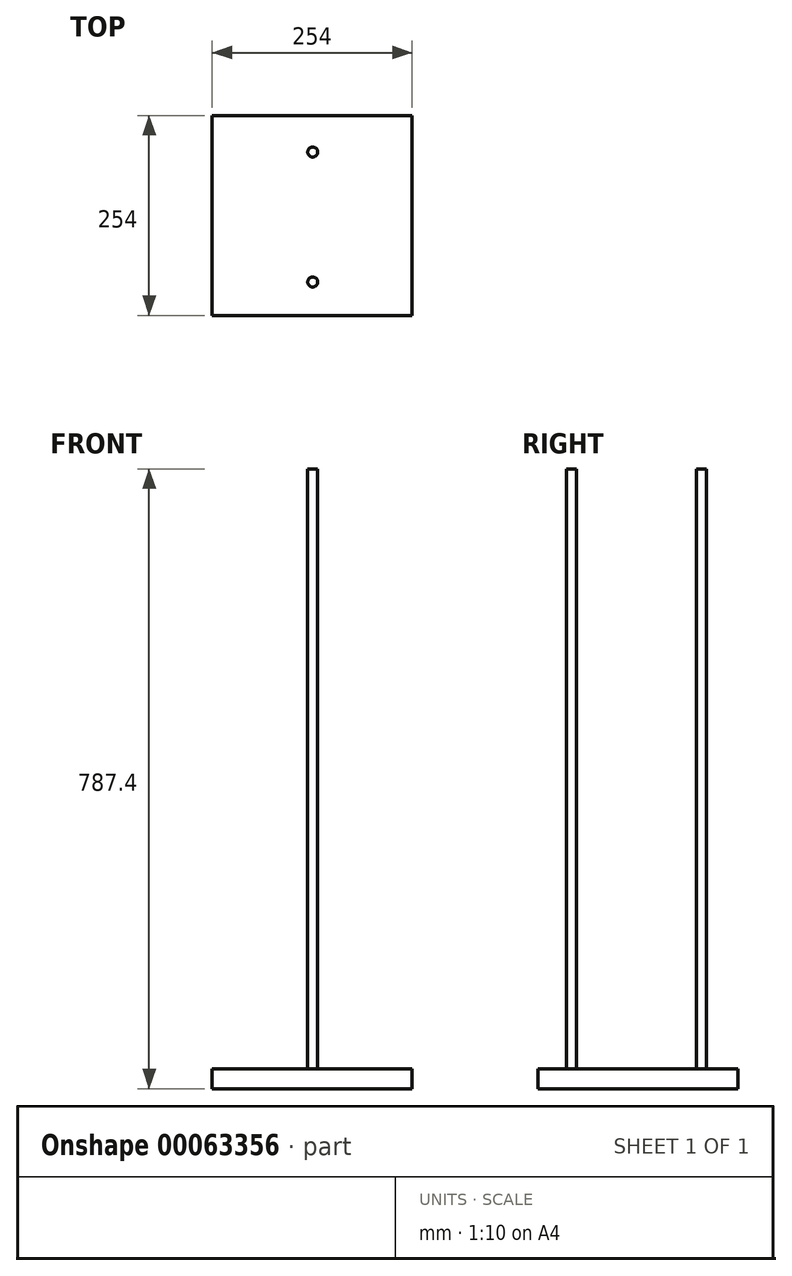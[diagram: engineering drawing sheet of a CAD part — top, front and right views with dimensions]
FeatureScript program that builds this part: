
annotation { "Feature Type Name" : "Feature", "Feature Type Description" : "" }
export const myFeature = defineFeature(function(context is Context, id is Id, definition is map)
    precondition{}
    {
        {
            var Q0;
            Q0=qCreatedBy(makeId("Top.planeOp"),FACE);
            var sketch = newSketch(context, id + "F0", { "sketchPlane" : qUnion([Q0])});
            skLineSegment(sketch, "E0.bottom", {"start": v(-127.78, 129.03) * mm, "end": v(126.22, 129.03) * mm});
            skLineSegment(sketch, "E0.top", {"start": v(-127.78, -124.97) * mm, "end": v(126.22, -124.97) * mm});
            skLineSegment(sketch, "E0.left", {"start": v(-127.78, 129.03) * mm, "end": v(-127.78, -124.97) * mm});
            skLineSegment(sketch, "E0.right", {"start": v(126.22, 129.03) * mm, "end": v(126.22, -124.97) * mm});
            skSolve(sketch);
        }
        {
            var Q0;
            Q0 = qSketchRegion(id + "F0", true);
            extrude(context, id + "F1", {"entities" : qUnion([Q0]), "endBound" : BoundingType.SYMMETRIC, "depth" : 25.4 * mm});
        }
        {
            var Q0;
            Q0=makeQuery(id+"F1.opExtrude","CAP_FACE",FACE,{"disambiguationData":[OSD([sQuery(id+"F0.wireOp",EDGE,"E0.bottom"),sQuery(id+"F0.wireOp",EDGE,"E0.top"),sQuery(id+"F0.wireOp",EDGE,"E0.left"),sQuery(id+"F0.wireOp",EDGE,"E0.right")])],"isStart":false});
            var sketch = newSketch(context, id + "F2", { "sketchPlane" : qUnion([Q0])});
            skCircle(sketch, "E1", {"center": v(0, -82.55) * mm, "radius": 6.35 * mm});
            skCircle(sketch, "E2", {"center": v(0, 82.55) * mm, "radius": 6.35 * mm});
            skSolve(sketch);
        }
        {
            var Q0;
            Q0 = qSketchRegion(id + "F2", true);
            extrude(context, id + "F3", {"entities" : qUnion([Q0]), "operationType" : NewBodyOperationType.ADD, "depth" : 762 * mm});
        }
        {
            var Q0;
            Q0=qCreatedBy(makeId("Right.planeOp"),FACE);
            var sketch = newSketch(context, id + "F4", { "sketchPlane" : qUnion([Q0])});
            skLineSegment(sketch, "E3", {"start": v(-76.2, 787.4) * mm, "end": v(-76.2, 25.4) * mm, "construction": true});
            skLineSegment(sketch, "E4", {"start": v(76.2, 25.4) * mm, "end": v(76.2, 787.4) * mm, "construction": true});
            skSolve(sketch);
        }
    });
